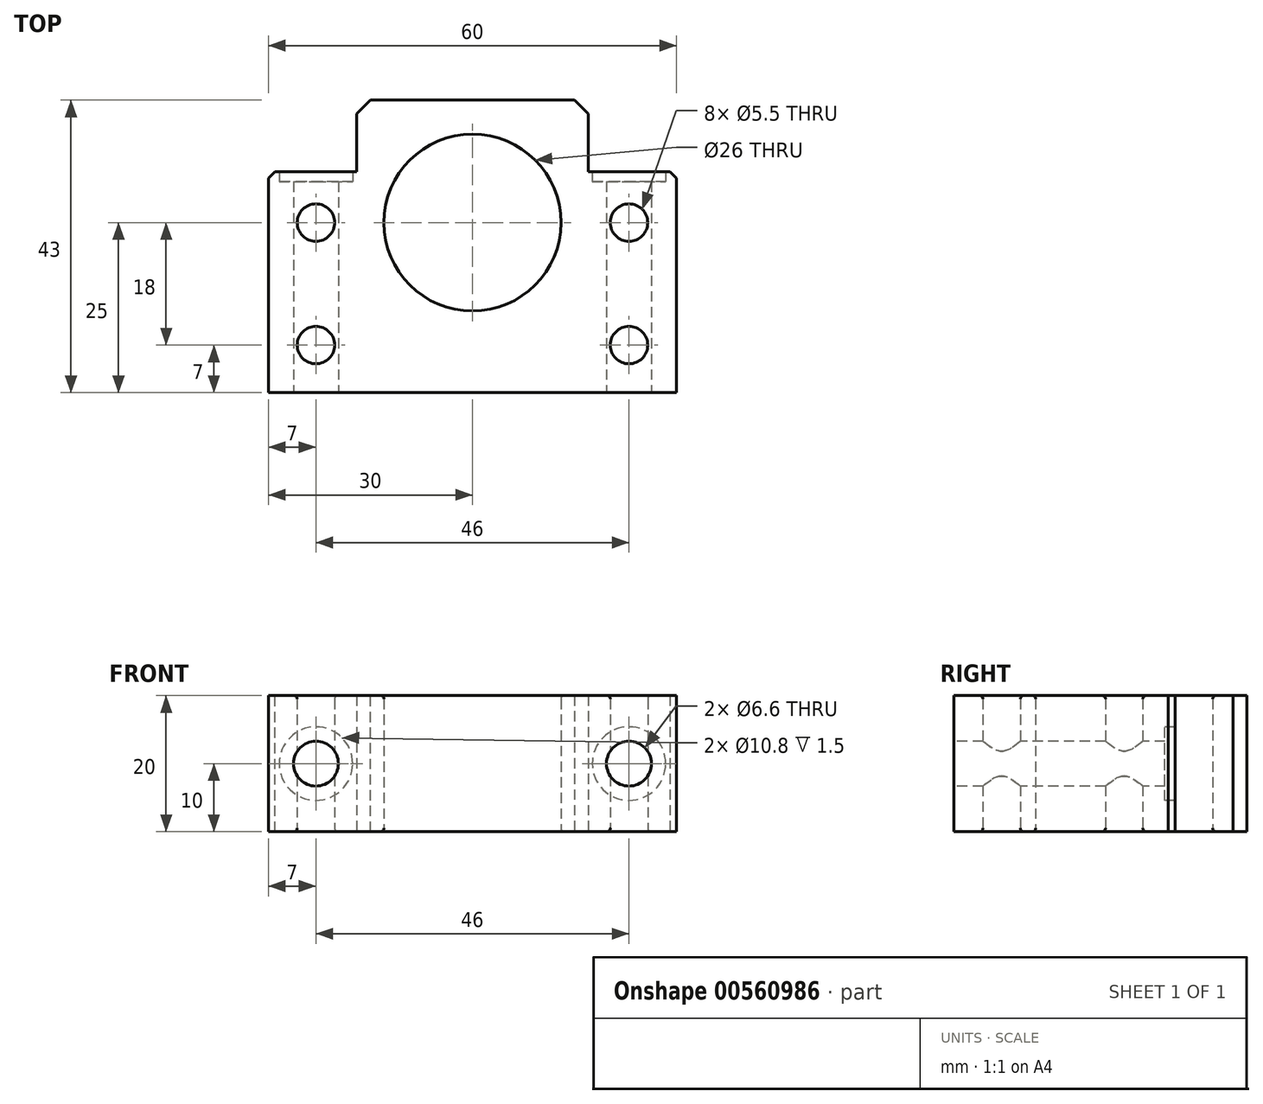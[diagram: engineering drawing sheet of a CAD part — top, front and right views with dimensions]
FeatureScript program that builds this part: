
annotation { "Feature Type Name" : "Feature", "Feature Type Description" : "" }
export const myFeature = defineFeature(function(context is Context, id is Id, definition is map)
    precondition{}
    {
        {
            var Q0;
            Q0=qCreatedBy(makeId("Top.planeOp"),FACE);
            var sketch = newSketch(context, id + "F0", { "sketchPlane" : qUnion([Q0])});
            skLineSegment(sketch, "E0", {"start": v(-30, -25) * mm, "end": v(30, -25) * mm});
            skLineSegment(sketch, "E1", {"start": v(30, -25) * mm, "end": v(30, 7.5) * mm});
            skLineSegment(sketch, "E2", {"start": v(30, 7.5) * mm, "end": v(17, 7.5) * mm});
            skLineSegment(sketch, "E3", {"start": v(17, 7.5) * mm, "end": v(17, 18) * mm});
            skLineSegment(sketch, "E4", {"start": v(17, 18) * mm, "end": v(-17, 18) * mm});
            skLineSegment(sketch, "E5", {"start": v(-17, 18) * mm, "end": v(-17, 7.5) * mm});
            skLineSegment(sketch, "E6", {"start": v(-17, 7.5) * mm, "end": v(-30, 7.5) * mm});
            skLineSegment(sketch, "E7", {"start": v(-30, 7.5) * mm, "end": v(-30, -25) * mm});
            skPoint(sketch, "E8", {"position": v(23, 0) * mm});
            skPoint(sketch, "E9", {"position": v(23, -18) * mm});
            skPoint(sketch, "E10", {"position": v(-23, 0) * mm});
            skPoint(sketch, "E11", {"position": v(-23, -18) * mm});
            skCircle(sketch, "E12", {"center": v(-23, 0) * mm, "radius": 2.75 * mm});
            skCircle(sketch, "E13.MirrorC", {"center": v(23, 0) * mm, "radius": 2.75 * mm});
            skCircle(sketch, "E14", {"center": v(-23, -18) * mm, "radius": 2.75 * mm});
            skCircle(sketch, "E15.MirrorC", {"center": v(23, -18) * mm, "radius": 2.75 * mm});
            skCircle(sketch, "E16", {"center": v(0, 0) * mm, "radius": 13 * mm});
            skSolve(sketch);
        }
        {
            var Q0;
            Q0=makeQuery(id+"F0.imprint","IMPRINT",FACE,{"disambiguationData":[TD([[makeQuery(id+"F0.imprint","IMPRINT",EDGE,{"derivedFrom":sQuery(id+"F0.wireOp",EDGE,"E0")}),1.0]])]});
            extrude(context, id + "F1", {"entities" : qUnion([Q0]), "depth" : 10 * mm, "offsetDistance" : 25 * mm, "hasSecondDirection" : true, "secondDirectionOppositeDirection" : true, "secondDirectionDepth" : 10 * mm});
        }
        {
            var Q0;
            Q0=makeQuery(id+"F1.opExtrude","SWEPT_EDGE",EDGE,{"disambiguationData":[OSD([sQuery(id+"F0.wireOp",EDGE,"E1"),sQuery(id+"F0.wireOp",EDGE,"E2")])]});
            var Q1;
            Q1=makeQuery(id+"F1.opExtrude","SWEPT_EDGE",EDGE,{"disambiguationData":[OSD([sQuery(id+"F0.wireOp",EDGE,"E6"),sQuery(id+"F0.wireOp",EDGE,"E7")])]});
            chamfer(context, id + "F2", {"entities" : qUnion([Q0, Q1]), "width" : 1 * mm, "tangentPropagation" : true});
        }
        {
            var Q0;
            Q0=makeQuery(id+"F1.opExtrude","SWEPT_EDGE",EDGE,{"disambiguationData":[OSD([sQuery(id+"F0.wireOp",EDGE,"E3"),sQuery(id+"F0.wireOp",EDGE,"E4")])]});
            var Q1;
            Q1=makeQuery(id+"F1.opExtrude","SWEPT_EDGE",EDGE,{"disambiguationData":[OSD([sQuery(id+"F0.wireOp",EDGE,"E4"),sQuery(id+"F0.wireOp",EDGE,"E5")])]});
            chamfer(context, id + "F3", {"entities" : qUnion([Q0, Q1]), "width" : 2 * mm, "tangentPropagation" : true});
        }
        {
            var Q0;
            Q0=makeQuery(id+"F1.opExtrude","SWEPT_FACE",FACE,{"disambiguationData":[OSD([sQuery(id+"F0.wireOp",EDGE,"E12")])]});
            var Q1;
            Q1=makeQuery(id+"F1.opExtrude","SWEPT_FACE",FACE,{"disambiguationData":[OSD([sQuery(id+"F0.wireOp",EDGE,"E13.MirrorC")])]});
            var Q2;
            Q2=makeQuery(id+"F1.opExtrude","SWEPT_FACE",FACE,{"disambiguationData":[OSD([sQuery(id+"F0.wireOp",EDGE,"E15.MirrorC")])]});
            var Q3;
            Q3=makeQuery(id+"F1.opExtrude","SWEPT_FACE",FACE,{"disambiguationData":[OSD([sQuery(id+"F0.wireOp",EDGE,"E14")])]});
            var Q4;
            Q4=makeQuery(id+"F1.opExtrude","SWEPT_FACE",FACE,{"disambiguationData":[OSD([sQuery(id+"F0.wireOp",EDGE,"E16")])]});
            fillet(context, id + "F4", {"entities" : qUnion([Q0, Q1, Q2, Q3, Q4]), "radius" : .5 * mm, "tangentPropagation" : true, "allowEdgeOverflow" : false});
        }
        {
            var Q0;
            Q0=makeQuery(id+"F1.opExtrude","SWEPT_FACE",FACE,{"disambiguationData":[OSD([sQuery(id+"F0.wireOp",EDGE,"E2")])]});
            cPlane(context, id + "F5", {"entities" : qUnion([Q0]), "cplaneType" : CPlaneType.OFFSET, "offset" : 0 * mm, "width" : 150 * mm, "height" : 150 * mm});
        }
        {
            var Q0;
            Q0=qCreatedBy(id+"F5.planeOp",FACE);
            var sketch = newSketch(context, id + "F6", { "sketchPlane" : qUnion([Q0])});
            skPoint(sketch, "E17", {"position": v(-23, 0) * mm});
            skPoint(sketch, "E18.MirrorP", {"position": v(23, 0) * mm});
            skSolve(sketch);
        }
        {
            var Q0;
            Q0=sQuery(id+"F6.wireOp",VERTEX,"E17");
            var Q1;
            Q1=sQuery(id+"F6.wireOp",VERTEX,"E18.MirrorP");
            var Q2;
            Q2=makeQuery(id+"F1.opExtrude","SWEPT_BODY",BODY,{"disambiguationData":[OSD([sQuery(id+"F0.wireOp",EDGE,"E0"),sQuery(id+"F0.wireOp",EDGE,"E1"),sQuery(id+"F0.wireOp",EDGE,"E2"),sQuery(id+"F0.wireOp",EDGE,"E3"),sQuery(id+"F0.wireOp",EDGE,"E4"),sQuery(id+"F0.wireOp",EDGE,"E5"),sQuery(id+"F0.wireOp",EDGE,"E6"),sQuery(id+"F0.wireOp",EDGE,"E7"),sQuery(id+"F0.wireOp",EDGE,"E12"),sQuery(id+"F0.wireOp",EDGE,"E13.MirrorC"),sQuery(id+"F0.wireOp",EDGE,"E14"),sQuery(id+"F0.wireOp",EDGE,"E15.MirrorC")])]});
            hole(context, id + "F7", {"style" : HoleStyle.C_BORE, "endStyle" : HoleEndStyle.THROUGH, "holeDiameter" : 6.6 * mm, "cBoreDiameter" : 10.8 * mm, "cBoreDepth" : 1.5 * mm, "isTappedThrough" : true, "tappedDepth" : 12 * mm, "tapClearance" : 3, "locations" : qUnion([Q0, Q1]), "scope" : qUnion([Q2]), "startStyle" : HoleStartStyle.SKETCH});
        }
    });
